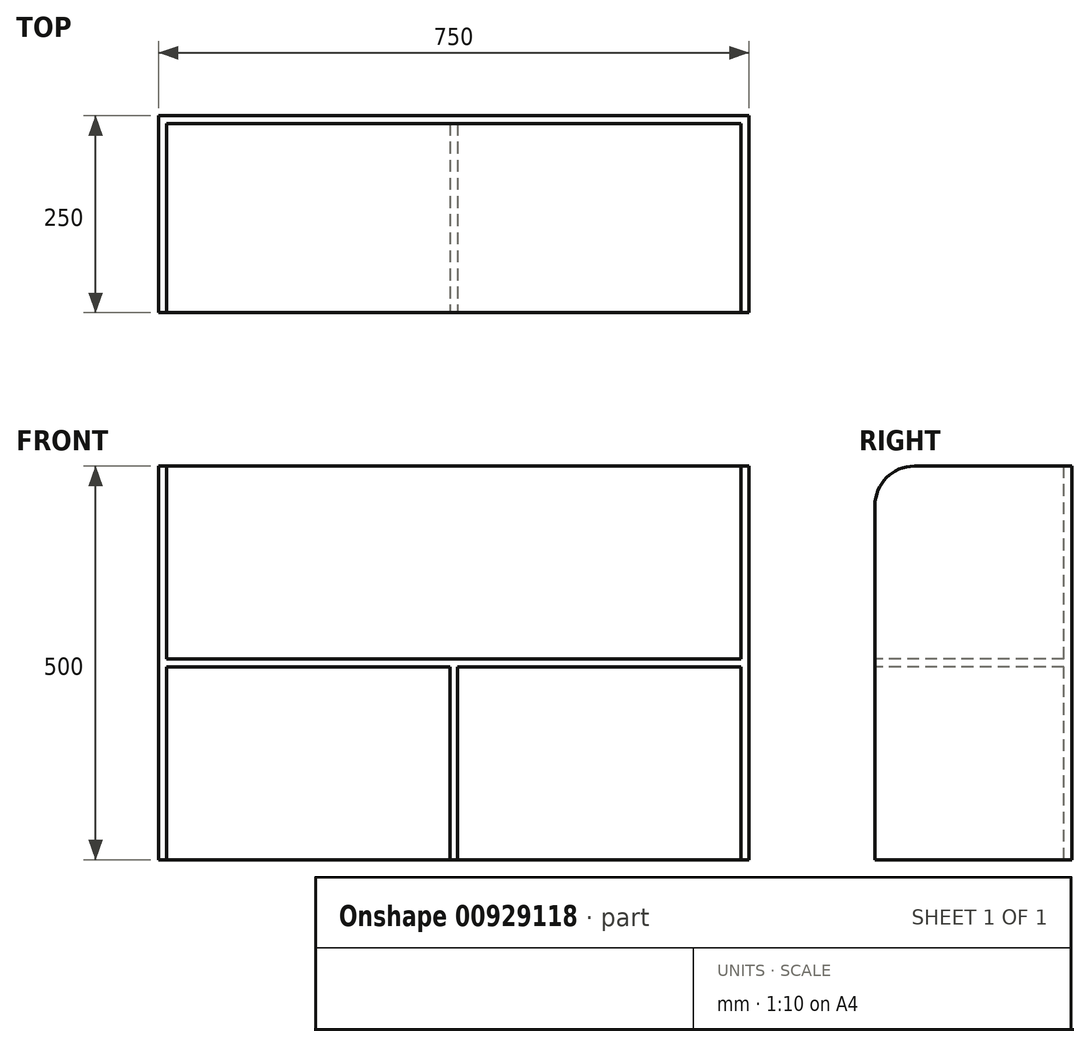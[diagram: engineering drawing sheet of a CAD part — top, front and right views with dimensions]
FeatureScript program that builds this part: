
annotation { "Feature Type Name" : "Feature", "Feature Type Description" : "" }
export const myFeature = defineFeature(function(context is Context, id is Id, definition is map)
    precondition{}
    {
        {
            var Q0;
            Q0=qCreatedBy(makeId("Front.planeOp"),FACE);
            var sketch = newSketch(context, id + "F0", { "sketchPlane" : qUnion([Q0])});
            skLineSegment(sketch, "E0.bottom", {"start": v(-375, 0) * mm, "end": v(375, 0) * mm});
            skLineSegment(sketch, "E0.top", {"start": v(-375, 250) * mm, "end": v(375, 250) * mm});
            skLineSegment(sketch, "E0.left", {"start": v(-375, 0) * mm, "end": v(-375, 250) * mm});
            skLineSegment(sketch, "E0.right", {"start": v(375, 0) * mm, "end": v(375, 250) * mm});
            skSolve(sketch);
        }
        {
            var Q0;
            Q0=qSketchRegion(id+"F0",true);
            extrude(context, id + "F1", {"entities" : qUnion([Q0]), "depth" : -250 * mm, "offsetDistance" : 25 * mm});
        }
        {
            var Q0;
            Q0=makeQuery(id+"F1.opExtrude","SWEPT_BODY",BODY,{"disambiguationData":[OSD([sQuery(id+"F0.wireOp",EDGE,"E0.bottom"),sQuery(id+"F0.wireOp",EDGE,"E0.top"),sQuery(id+"F0.wireOp",EDGE,"E0.left"),sQuery(id+"F0.wireOp",EDGE,"E0.right")])]});
            var Q1;
            Q1=qCreatedBy(makeId("Top.planeOp"),FACE);
            mirror(context, id + "F2", {"operationType" : NewBodyOperationType.ADD, "entities" : qUnion([Q0]), "mirrorPlane" : qUnion([Q1])});
        }
        {
            var Q0;
            {var subQ0=makeQuery(id+"F1.opExtrude","CAP_FACE",FACE,{"disambiguationData":[OSD([sQuery(id+"F0.wireOp",EDGE,"E0.bottom"),sQuery(id+"F0.wireOp",EDGE,"E0.top"),sQuery(id+"F0.wireOp",EDGE,"E0.left"),sQuery(id+"F0.wireOp",EDGE,"E0.right")])],"isStart":true});Q0=makeQuery(id+"F2.boolean.opBoolean","MERGE",FACE,{"derivedFrom":[subQ0,makeQuery(id+"F2.opPattern","COPY",FACE,{"derivedFrom":subQ0,"instanceName":"1"})]});}
            var Q1;
            Q1=makeQuery(id+"F1.opExtrude","SWEPT_FACE",FACE,{"disambiguationData":[OSD([sQuery(id+"F0.wireOp",EDGE,"E0.top")])]});
            var Q2;
            Q2=makeQuery(id+"F2.opPattern","COPY",FACE,{"derivedFrom":makeQuery(id+"F1.opExtrude","SWEPT_FACE",FACE,{"disambiguationData":[OSD([sQuery(id+"F0.wireOp",EDGE,"E0.top")])]}),"instanceName":"1"});
            shell(context, id + "F3", {"entities" : qUnion([Q0, Q1, Q2]), "thickness" : 10 * mm});
        }
        {
            var Q0;
            Q0=qCreatedBy(makeId("Top.planeOp"),FACE);
            var sketch = newSketch(context, id + "F4", { "sketchPlane" : qUnion([Q0])});
            skPoint(sketch, "E1.0", {"position": v(-365, 240) * mm});
            skPoint(sketch, "E2.0", {"position": v(365, 0) * mm});
            skLineSegment(sketch, "E3.bottom", {"start": v(-365, 240) * mm, "end": v(365, 240) * mm});
            skLineSegment(sketch, "E3.top", {"start": v(-365, 0) * mm, "end": v(365, 0) * mm});
            skLineSegment(sketch, "E3.left", {"start": v(-365, 240) * mm, "end": v(-365, 0) * mm});
            skLineSegment(sketch, "E3.right", {"start": v(365, 240) * mm, "end": v(365, 0) * mm});
            skSolve(sketch);
        }
        {
            var Q0;
            Q0=qSketchRegion(id+"F4",true);
            extrude(context, id + "F5", {"entities" : qUnion([Q0]), "operationType" : NewBodyOperationType.ADD, "endBound" : BoundingType.SYMMETRIC, "depth" : 10 * mm, "offsetDistance" : 25 * mm});
        }
        {
            var Q0;
            Q0=makeQuery(id+"F1.opExtrude","CAP_EDGE",EDGE,{"disambiguationData":[OSD([sQuery(id+"F0.wireOp",EDGE,"E0.top")])],"isStart":true});
            fillet(context, id + "F6", {"entities" : qUnion([Q0]), "radius" : 50 * mm, "tangentPropagation" : true, "allowEdgeOverflow" : false});
        }
        {
            var Q0;
            {var subQ0=sQuery(id+"F0.wireOp",EDGE,"E0.top");Q0=makeQuery(id+"F3.opShell","OFFSET_EDGE",EDGE,{"disambiguationData":[OSD([subQ0]),TDD([makeQuery(id+"F1.opExtrude","CAP_EDGE",EDGE,{"disambiguationData":[OSD([subQ0])],"isStart":true})])]});}
            fillet(context, id + "F7", {"entities" : qUnion([Q0]), "radius" : 50 * mm, "tangentPropagation" : true, "allowEdgeOverflow" : false});
        }
        {
            var Q0;
            Q0=qCreatedBy(makeId("Right.planeOp"),FACE);
            var sketch = newSketch(context, id + "F8", { "sketchPlane" : qUnion([Q0])});
            skLineSegment(sketch, "E4.0", {"start": v(0, -250) * mm, "end": v(0, -5) * mm});
            skLineSegment(sketch, "E5.0", {"start": v(240, -250) * mm, "end": v(0, -250) * mm});
            skLineSegment(sketch, "E6.0", {"start": v(240, -5) * mm, "end": v(0, -5) * mm});
            skLineSegment(sketch, "E7.0", {"start": v(240, -250) * mm, "end": v(240, -5) * mm});
            skSolve(sketch);
        }
        {
            var Q0;
            Q0 = qSketchRegion(id + "F8", true);
            extrude(context, id + "F9", {"entities" : qUnion([Q0]), "operationType" : NewBodyOperationType.ADD, "endBound" : BoundingType.SYMMETRIC, "depth" : 10 * mm, "offsetDistance" : 25 * mm});
        }
    });
